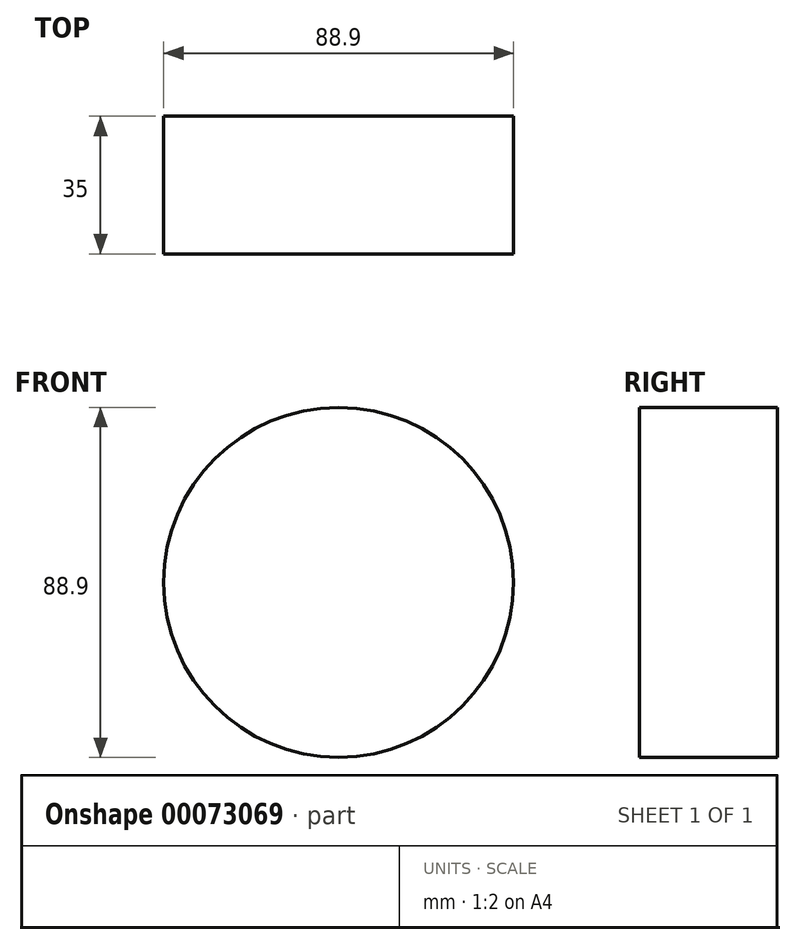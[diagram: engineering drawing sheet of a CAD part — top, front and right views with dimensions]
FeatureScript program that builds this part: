
annotation { "Feature Type Name" : "Feature", "Feature Type Description" : "" }
export const myFeature = defineFeature(function(context is Context, id is Id, definition is map)
    precondition{}
    {
        {
            var Q0;
            Q0=qCreatedBy(makeId("Front.planeOp"),FACE);
            var sketch = newSketch(context, id + "F0", { "sketchPlane" : qUnion([Q0])});
            skCircle(sketch, "E0", {"center": v(0, 0) * mm, "radius": 44.45 * mm});
            skSolve(sketch);
        }
        {
            var Q0;
            Q0 = qSketchRegion(id + "F0", true);
            extrude(context, id + "F1", {"entities" : qUnion([Q0]), "depth" : 35 * mm});
        }
    });
